# Revit family: Sink-Top_Mount-Kohler-Dickinson-6546X
name_source: partatom
category: Plumbing Fixtures
revit_build: Autodesk Revit MEP 2012 (Build: 20110916_2132(x64)
units: mm (PartAtom-declared; Revit-internal decimal feet)

## types (4) — shared parameters
Date Modified = March 13, 2015
Depth = 22.125 "
Description = See Part Description
Drain Flow = 0 GPM
Drain Radius = 0.625 "
Equipment Abbreviation = DSS
Family Version = 1.0
Height = 8.75 "
Manufacturer = Kohler Company
Model = See Part Number
Model Disclaimer = Contact Kohler Company For More Information
Product Page URL = http://www.us.kohler.com
URL = http://www.us.kohler.com
Width = 33 "
zz Length 1 = 33 "
zz Length 2 = 30 "
zz Length 3 = 8.75 "
zz Length 6 = 22.125 "

## per-type parameters (varying)
| type | Product Material | zz Integer 2 |
| White | Cast Iron - Kohler - White Enamel | 1 |
| Biscuit | Cast Iron - Kohler - Biscuit Enamel | 2 |
| Almond | Cast Iron - Kohler - Almond Enamel | 3 |
| Black | Cast Iron - Kohler - Black Enamel | 4 |

## geometry (parser evidence)
native form markers: Blend x2, Sweep x2
no freeform markers — native parametric forms only
